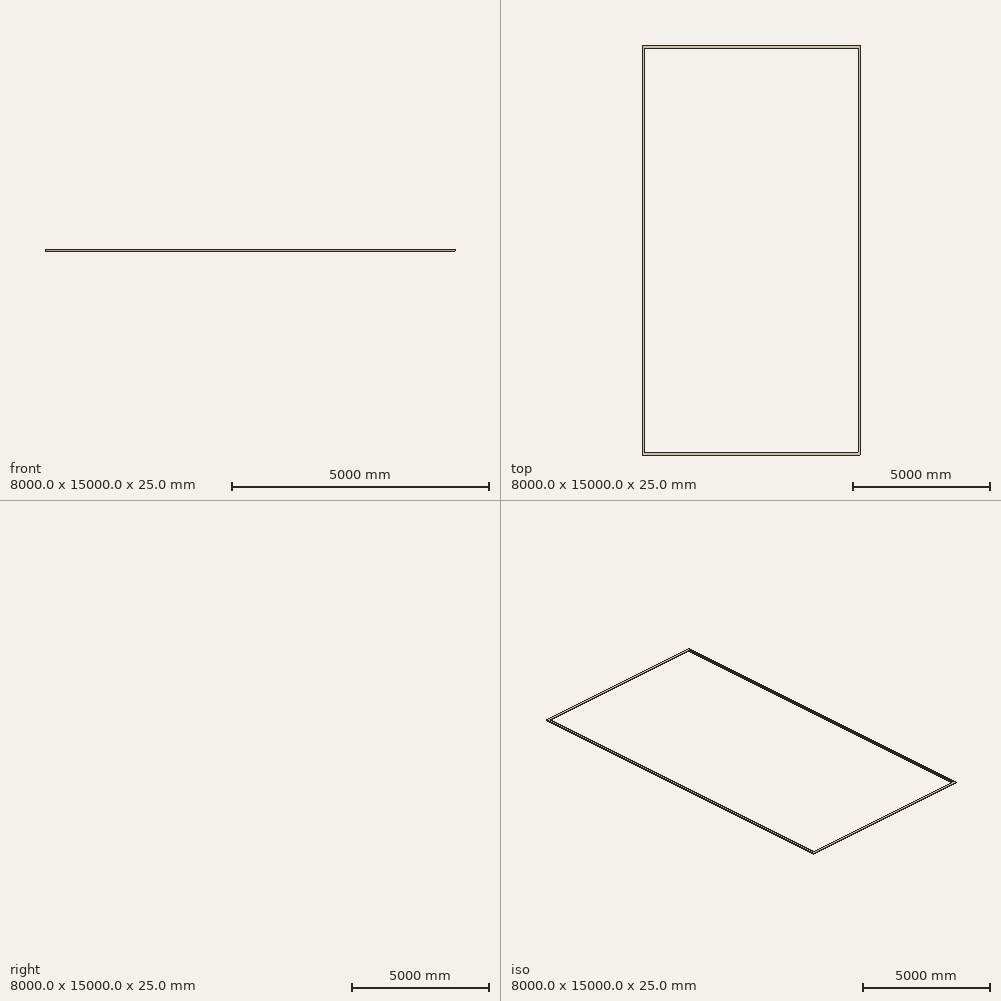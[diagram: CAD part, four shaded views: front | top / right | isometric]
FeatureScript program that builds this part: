
annotation { "Feature Type Name" : "Feature", "Feature Type Description" : "" }
export const myFeature = defineFeature(function(context is Context, id is Id, definition is map)
    precondition{}
    {
        {
            var Q0;
            Q0=qCreatedBy(makeId("Top.planeOp"),FACE);
            var sketch = newSketch(context, id + "F0", { "sketchPlane" : qUnion([Q0])});
            skLineSegment(sketch, "E0.bottom", {"start": v(0, 0) * mm, "end": v(-8000, 0) * mm});
            skLineSegment(sketch, "E0.top", {"start": v(0, 15000) * mm, "end": v(-8000, 15000) * mm});
            skLineSegment(sketch, "E0.left", {"start": v(0, 0) * mm, "end": v(0, 15000) * mm});
            skLineSegment(sketch, "E0.right", {"start": v(-8000, 0) * mm, "end": v(-8000, 15000) * mm});
            skLineSegment(sketch, "E1.0", {"start": v(0, 14900) * mm, "end": v(-10000, 14900) * mm});
            skLineSegment(sketch, "E2.0", {"start": v(-100, 0) * mm, "end": v(-100, 17000) * mm});
            skLineSegment(sketch, "E3.0", {"start": v(0, 100) * mm, "end": v(-10000, 100) * mm});
            skLineSegment(sketch, "E4.0", {"start": v(-7900, 0) * mm, "end": v(-7900, 17000) * mm});
            skSolve(sketch);
        }
        {
            var Q0;
            Q0 = qSketchRegion(id + "F0", true);
            extrude(context, id + "F1", {"entities" : qUnion([Q0]), "depth" : 25 * mm});
        }
    });
